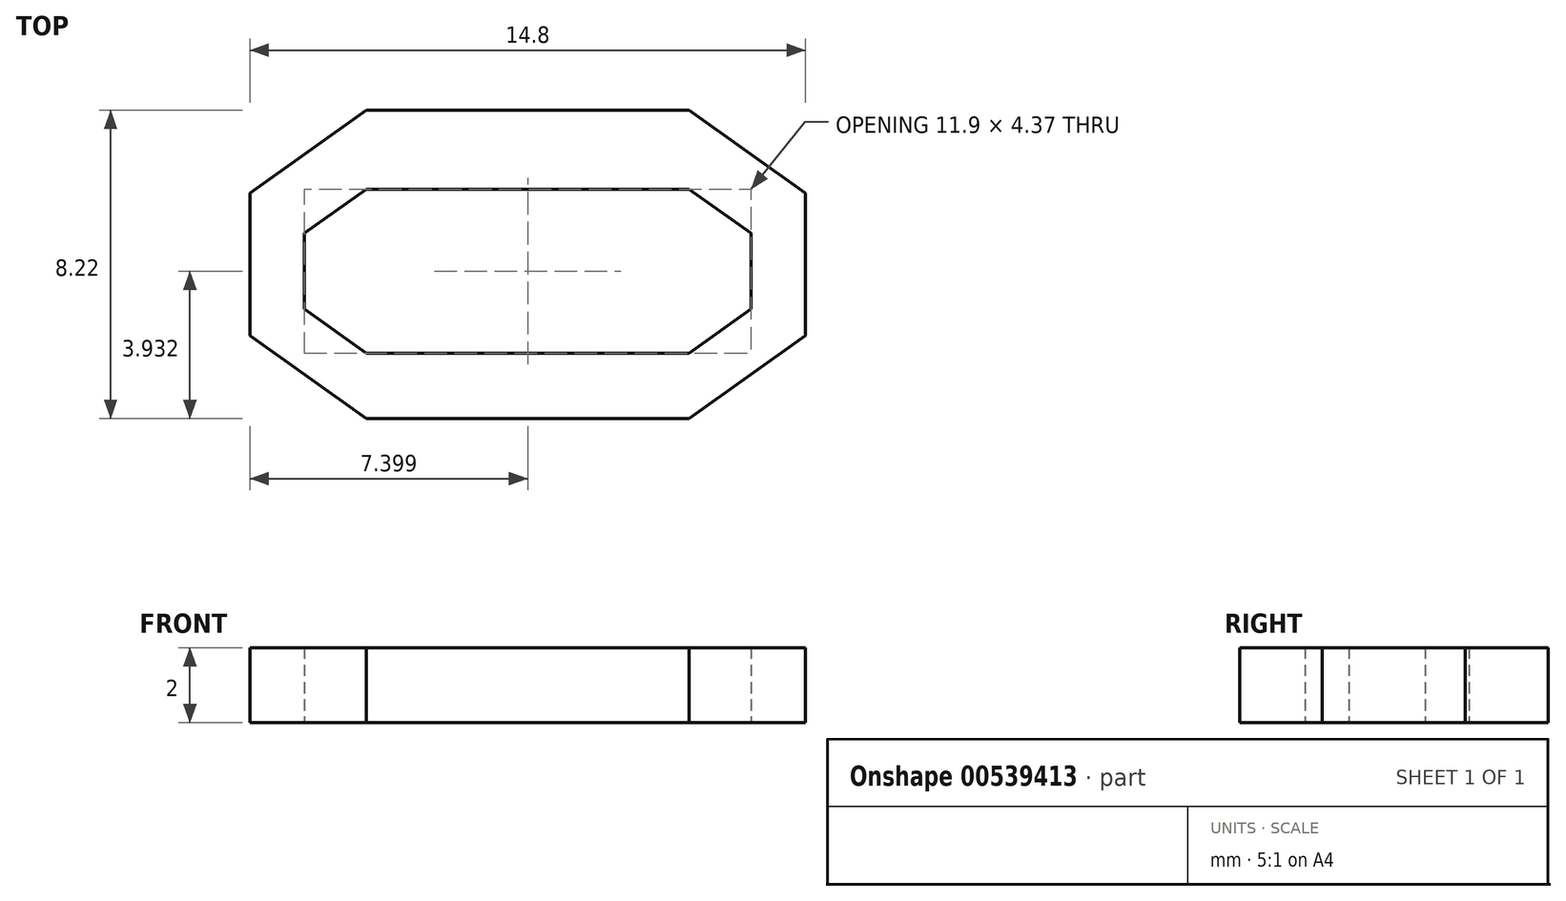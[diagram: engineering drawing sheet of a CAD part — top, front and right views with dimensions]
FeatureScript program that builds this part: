
annotation { "Feature Type Name" : "Feature", "Feature Type Description" : "" }
export const myFeature = defineFeature(function(context is Context, id is Id, definition is map)
    precondition{}
    {
        {
            var Q0;
            Q0=qCreatedBy(makeId("Top.planeOp"),FACE);
            var sketch = newSketch(context, id + "F0", { "sketchPlane" : qUnion([Q0])});
            skLineSegment(sketch, "E0", {"start": v(-8.6, 0) * mm, "end": v(-11.7, 2.2) * mm});
            skLineSegment(sketch, "E1", {"start": v(-11.7, 2.2) * mm, "end": v(-11.7, 6.01) * mm});
            skLineSegment(sketch, "E2", {"start": v(-11.7, 6.01) * mm, "end": v(-8.6, 8.22) * mm});
            skLineSegment(sketch, "E3", {"start": v(0, 8.22) * mm, "end": v(3.1, 6.01) * mm});
            skLineSegment(sketch, "E4", {"start": v(3.1, 6.01) * mm, "end": v(3.1, 2.2) * mm});
            skLineSegment(sketch, "E5", {"start": v(3.1, 2.2) * mm, "end": v(0, 0) * mm});
            skLineSegment(sketch, "E6", {"start": v(-8.6, 6.12) * mm, "end": v(-10.25, 4.94) * mm});
            skLineSegment(sketch, "E7", {"start": v(-10.25, 4.94) * mm, "end": v(-10.25, 2.92) * mm});
            skLineSegment(sketch, "E8", {"start": v(-10.25, 2.92) * mm, "end": v(-8.6, 1.75) * mm});
            skLineSegment(sketch, "E9", {"start": v(0, 1.75) * mm, "end": v(1.65, 2.92) * mm});
            skLineSegment(sketch, "E10", {"start": v(1.65, 2.92) * mm, "end": v(1.65, 4.94) * mm});
            skLineSegment(sketch, "E11", {"start": v(1.65, 4.94) * mm, "end": v(0, 6.12) * mm});
            skLineSegment(sketch, "E12", {"start": v(-8.6, 8.22) * mm, "end": v(0, 8.22) * mm});
            skLineSegment(sketch, "E13", {"start": v(-8.6, 6.12) * mm, "end": v(0, 6.12) * mm});
            skLineSegment(sketch, "E14", {"start": v(-8.6, 1.75) * mm, "end": v(0, 1.75) * mm});
            skLineSegment(sketch, "E15", {"start": v(0, 0) * mm, "end": v(-8.6, 0) * mm});
            skSolve(sketch);
        }
        {
            var Q0;
            Q0 = qSketchRegion(id + "F0", true);
            extrude(context, id + "F1", {"entities" : qUnion([Q0]), "depth" : 2 * mm, "offsetDistance" : 25.4 * mm});
        }
    });
